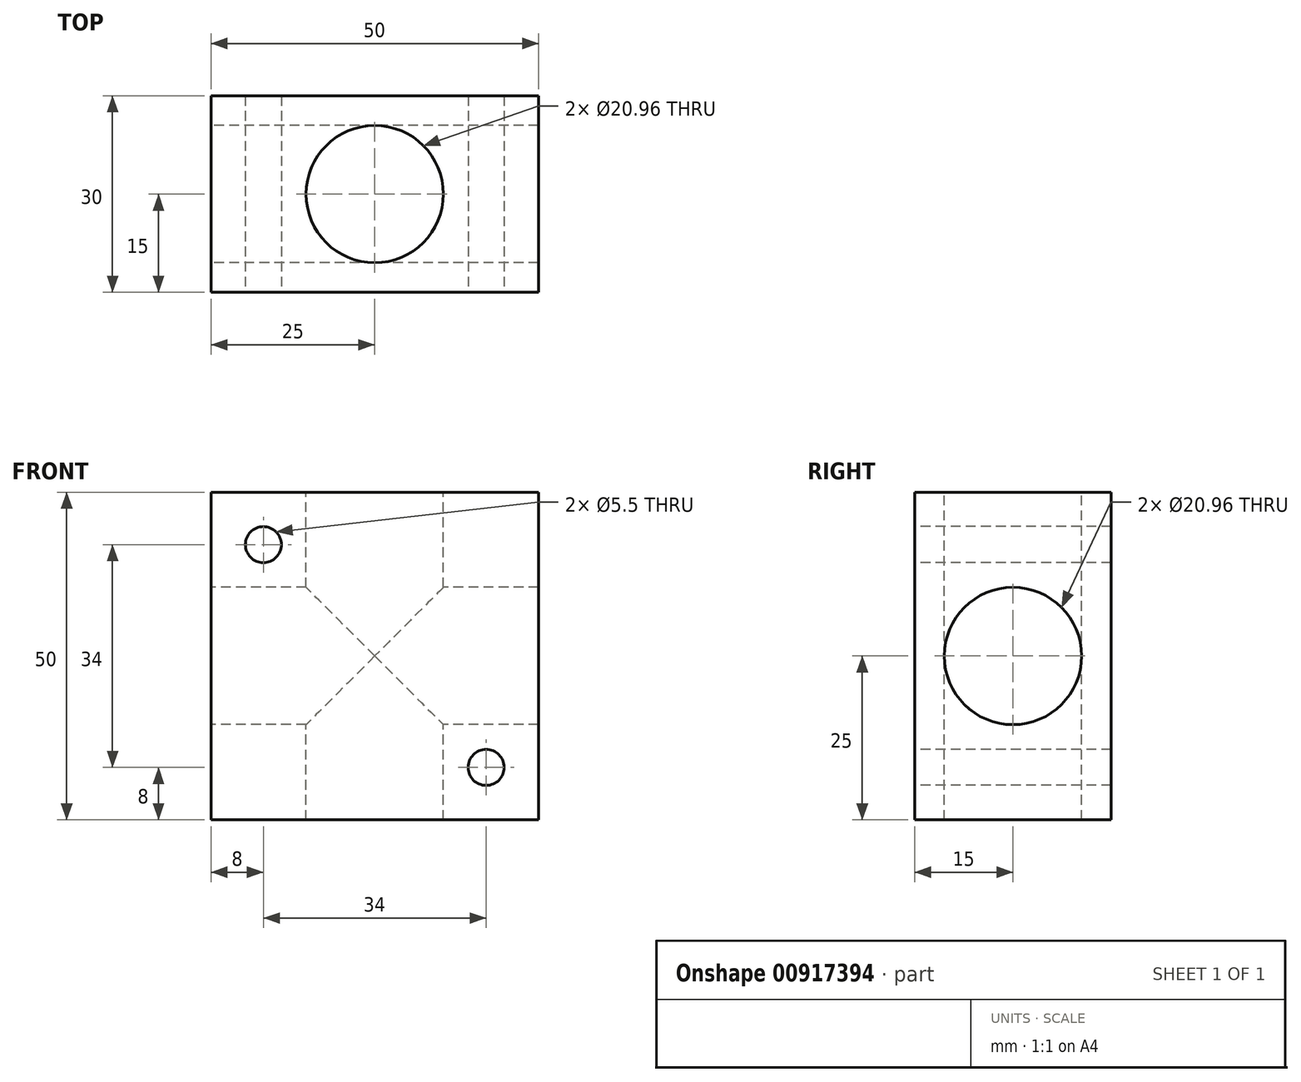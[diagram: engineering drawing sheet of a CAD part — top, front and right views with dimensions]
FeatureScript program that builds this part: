
annotation { "Feature Type Name" : "Feature", "Feature Type Description" : "" }
export const myFeature = defineFeature(function(context is Context, id is Id, definition is map)
    precondition{}
    {
        {
            var Q0;
            Q0=qCreatedBy(makeId("Front.planeOp"),FACE);
            var sketch = newSketch(context, id + "F0", { "sketchPlane" : qUnion([Q0])});
            skLineSegment(sketch, "E0.bottom", {"start": v(25, -25) * mm, "end": v(-25, -25) * mm});
            skLineSegment(sketch, "E0.top", {"start": v(25, 25) * mm, "end": v(-25, 25) * mm});
            skLineSegment(sketch, "E0.left", {"start": v(25, -25) * mm, "end": v(25, 25) * mm});
            skLineSegment(sketch, "E0.right", {"start": v(-25, -25) * mm, "end": v(-25, 25) * mm});
            skPoint(sketch, "E0.middle", {"position": v(0, 0) * mm});
            skSolve(sketch);
        }
        {
            var Q0;
            Q0=makeQuery(id+"F0.imprint","IMPRINT",FACE,{"disambiguationData":[TD([[makeQuery(id+"F0.imprint","IMPRINT",EDGE,{"derivedFrom":sQuery(id+"F0.wireOp",EDGE,"E0.bottom")}),-1.0]])]});
            extrude(context, id + "F1", {"entities" : qUnion([Q0]), "depth" : 30 * mm, "offsetDistance" : 25 * mm});
        }
        {
            var Q0;
            Q0=makeQuery(id+"F1.opExtrude","CAP_FACE",FACE,{"disambiguationData":[OSD([sQuery(id+"F0.wireOp",EDGE,"E0.bottom"),sQuery(id+"F0.wireOp",EDGE,"E0.top"),sQuery(id+"F0.wireOp",EDGE,"E0.left"),sQuery(id+"F0.wireOp",EDGE,"E0.right")])],"isStart":false});
            var sketch = newSketch(context, id + "F2", { "sketchPlane" : qUnion([Q0])});
            skPoint(sketch, "E1", {"position": v(-17, 17) * mm});
            skPoint(sketch, "E2", {"position": v(27.41, -27.38) * mm});
            skPoint(sketch, "E3", {"position": v(17, -17) * mm});
            skSolve(sketch);
        }
        {
            var Q0;
            Q0=sQuery(id+"F2.wireOp",VERTEX,"E1");
            var Q1;
            Q1=sQuery(id+"F2.wireOp",VERTEX,"E3");
            var Q2;
            Q2=makeQuery(id+"F1.opExtrude","SWEPT_BODY",BODY,{"disambiguationData":[OSD([sQuery(id+"F0.wireOp",EDGE,"E0.bottom"),sQuery(id+"F0.wireOp",EDGE,"E0.top"),sQuery(id+"F0.wireOp",EDGE,"E0.left"),sQuery(id+"F0.wireOp",EDGE,"E0.right")])]});
            hole(context, id + "F3", {"style" : HoleStyle.SIMPLE, "endStyle" : HoleEndStyle.THROUGH, "standardTappedOrClearance" : lookupTablePath({ "fit" : "Normal", "standard" : "ISO", "size" : "M5", "type" : "Clearance" }), "standardBlindInLast" : lookupTablePath({ "fit" : "Normal", "standard" : "ISO", "size" : "M5", "type" : "Clearance" }), "holeDiameter" : 5.5 * mm, "majorDiameter" : 5 * mm, "isTappedThrough" : true, "tappedDepth" : 5.5 * mm, "tapClearance" : 3, "locations" : qUnion([Q0, Q1]), "scope" : qUnion([Q2])});
        }
        {
            var Q0;
            Q0=makeQuery(id+"F1.opExtrude","SWEPT_FACE",FACE,{"disambiguationData":[OSD([sQuery(id+"F0.wireOp",EDGE,"E0.top")])]});
            var sketch = newSketch(context, id + "F4", { "sketchPlane" : qUnion([Q0])});
            skPoint(sketch, "E4", {"position": v(0, -15) * mm});
            skPoint(sketch, "E4.positionSnap0", {"position": v(-25, -15) * mm});
            skCircle(sketch, "E5", {"center": v(0, -15) * mm, "radius": 10.48 * mm});
            skSolve(sketch);
        }
        {
            var Q0;
            Q0=makeQuery(id+"F4.imprint","IMPRINT",FACE,{"disambiguationData":[TD([[makeQuery(id+"F4.imprint","IMPRINT",EDGE,{"derivedFrom":sQuery(id+"F4.wireOp",EDGE,"E5")}),1.0]])]});
            extrude(context, id + "F5", {"entities" : qUnion([Q0]), "operationType" : NewBodyOperationType.REMOVE, "endBound" : BoundingType.THROUGH_ALL, "oppositeDirection" : true, "depth" : 25 * mm, "offsetDistance" : 25 * mm});
        }
        {
            var Q0;
            Q0=makeQuery(id+"F1.opExtrude","SWEPT_FACE",FACE,{"disambiguationData":[OSD([sQuery(id+"F0.wireOp",EDGE,"E0.right")])]});
            var sketch = newSketch(context, id + "F6", { "sketchPlane" : qUnion([Q0])});
            skPoint(sketch, "E6", {"position": v(15, 0) * mm});
            skPoint(sketch, "E6.positionSnap0", {"position": v(15, 25) * mm});
            skCircle(sketch, "E7", {"center": v(15, 0) * mm, "radius": 10.48 * mm});
            skSolve(sketch);
        }
        {
            var Q0;
            Q0=makeQuery(id+"F6.imprint","IMPRINT",FACE,{"disambiguationData":[TD([[makeQuery(id+"F6.imprint","IMPRINT",EDGE,{"derivedFrom":sQuery(id+"F6.wireOp",EDGE,"E7")}),1.0]])]});
            extrude(context, id + "F7", {"entities" : qUnion([Q0]), "operationType" : NewBodyOperationType.REMOVE, "endBound" : BoundingType.THROUGH_ALL, "oppositeDirection" : true, "depth" : 25 * mm, "offsetDistance" : 25 * mm});
        }
    });
